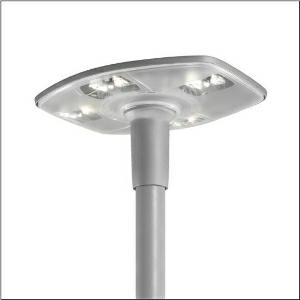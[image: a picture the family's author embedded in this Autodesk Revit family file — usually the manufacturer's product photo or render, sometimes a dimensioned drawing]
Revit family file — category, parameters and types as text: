
# Revit family: dl_r__30_led___st1_2c_5xa513281b08a5_eae4
name_source: partatom
category: Lighting Fixtures
units: mm (PartAtom-declared; Revit-internal decimal feet)

## family parameters
Cut with Voids When Loaded = No
Host = Face
Light Source = No
Part Type = Normal
Room Calculation Point = No
Round Connector Dimension = Use Diameter
Shared = No

## types (1)
- --- (1 x LED, 4590 lm, 49 W, 3000K)
    Apparent Load = 49 VA
    CIE Flux Codes = 32 71 98 100 100
    Color Rendering = 80
    Color Temperature = 3000K
    Default Elevation = 1800 mm
    Description = DL® 30 LED, mast luminaire, primary light control with 3 zone facetted reflector, of plastic, aluminium vaporised, highly specular, primary optical cover: cover, of PMMA, structured, transparent, light distribution: ST1.2c, light emission: direct distribution, primary light characteristic: asymmetric, crossroads, installation type: post-top, LED, High Power LED, rated luminous flux: 4.590lm, luminous efficacy: 94lm/W, light colour: 830, colour temperature: 3000K, control gear: Plus, control: flexible luminous flux parameterisation, time-dependent luminous flux control, constant luminous flux control, digital communication interface, power reduction, electronic power reduction, mains connection: 230..240V, AC, 50/60Hz, start of lifetime: 49W, end of service life: 51W, reduction: 22W, luminaire housing, of diecast aluminium, powder-coated, Siteco® metallic grey (DB 702S), length: 600mm, width: 510mm, height: 290mm, spigot size: d x l = 76 x 100mm (post-top) | with reducer (optional accessory) 60 x 100mm, mounting height: 3..6m, protection rating (complete): IP66, insulation class (complete): insulation class II (safety insulation), certification: CE, ENEC, VDE, impact resistance: IK08, permissible operating ambient temperature: -25..+30°C, standard-compliant lighting for roads and squares, packaging unit: 1 piece

Light Distribution: ST1.2c
    Height = 290 mm
    Lamp = 1 x LED
    Lamp Light Flux = 4590 lm
    Lamp Power = 49 W
    Lamp count = 1
    Length = 510 mm
    Luminous efficacy = 94 lm/W
    Manufacturer = Siteco
    ModVariant = No
    Model = 5XA513281B08A5
    Number of Poles = 1
    OnlyDefault = Yes
    Power Factor = 1
    Product Name = DL® 30 LED | ST1.2c
    Product group = mast luminaire | pylon top
    ProductGroupID = 6100
    Protection Class = Protection class II
    Protection Degree = IP 66
    RLX_Detail_Level = 1
    RLX_Emergency_Light_Flux = 0 lm
    RLX_Emergency_Type = 0
    RLX_Emergency_Type_DB = No
    RlxData = <blob elided: 86465 chars, md5=209b469f>
    Socket = socket
    Standby Power = 0 W
    System Light Flux = 4590 lm
    System Power = 49 W
    Type Comments = factory setting: luminous flux: 100 % | dim-lin: 254 | 497 mA
    Type Image = l_1006003.jpg
    URL = http://relux.com
    VarID = @adj_198180
    Voltage = 0 V
    Weight = 0.00 kg
    Width = 600 mm

## geometry (parser evidence)
native form markers: Blend x4, Sweep x12
no freeform markers — native parametric forms only
